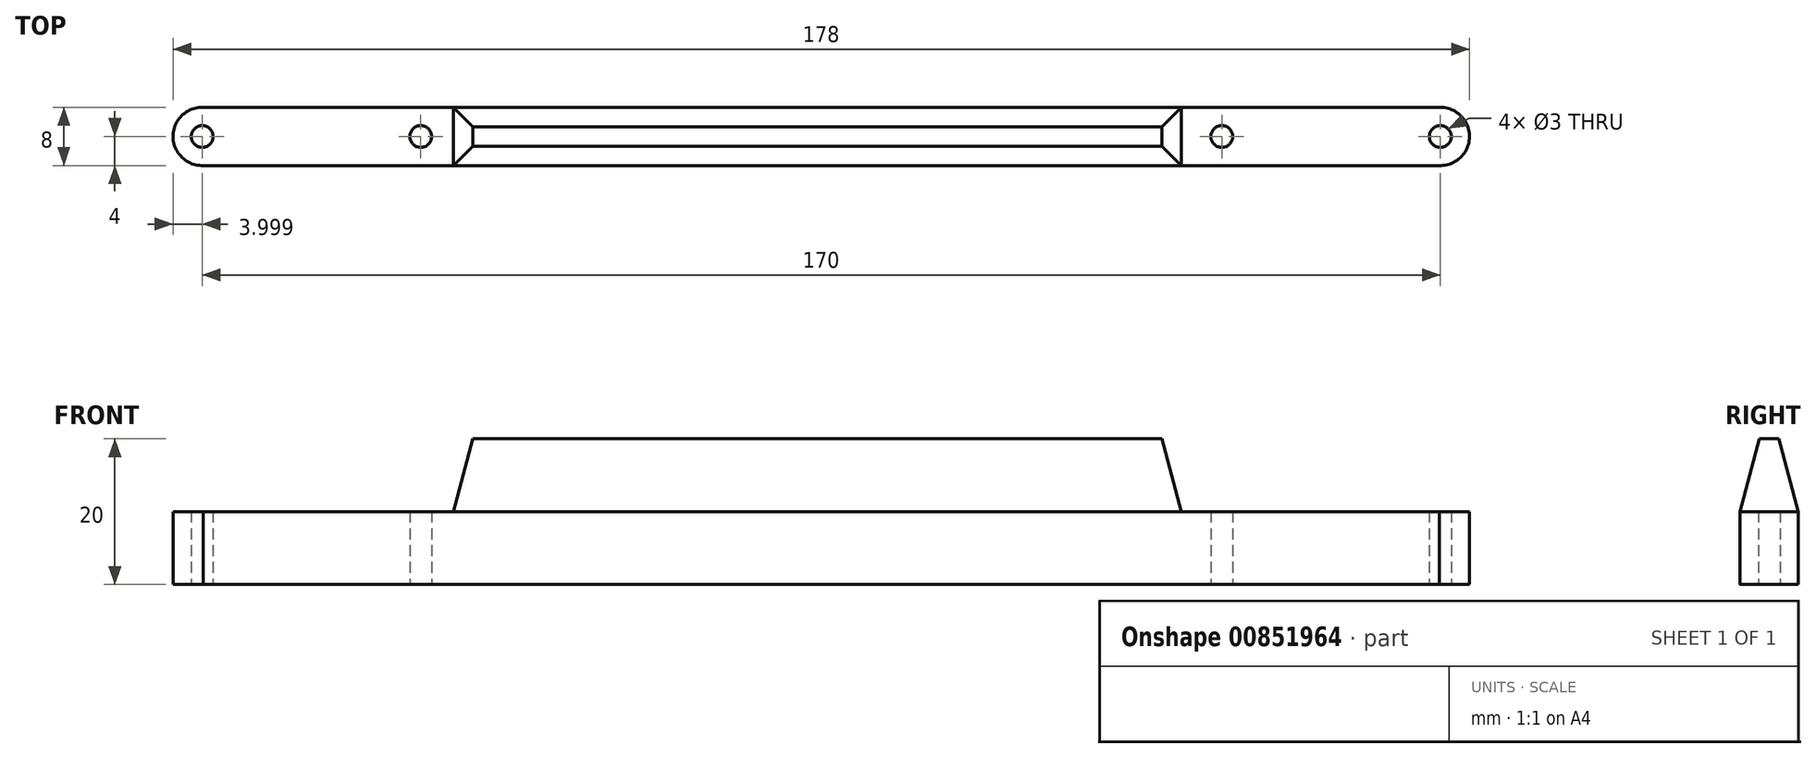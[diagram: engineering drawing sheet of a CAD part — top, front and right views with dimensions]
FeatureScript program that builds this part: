
annotation { "Feature Type Name" : "Feature", "Feature Type Description" : "" }
export const myFeature = defineFeature(function(context is Context, id is Id, definition is map)
    precondition{}
    {
        {
            var Q0;
            Q0=qCreatedBy(makeId("Top.planeOp"),FACE);
            var sketch = newSketch(context, id + "F0", { "sketchPlane" : qUnion([Q0])});
            skCircle(sketch, "E0", {"center": v(55.53, 0) * mm, "radius": 1.5 * mm});
            skCircle(sketch, "E1", {"center": v(-54.47, 0) * mm, "radius": 1.5 * mm});
            skCircle(sketch, "E2", {"center": v(85.53, 0) * mm, "radius": 1.5 * mm});
            skCircle(sketch, "E3", {"center": v(-84.47, 0) * mm, "radius": 1.5 * mm});
            skLineSegment(sketch, "E4", {"start": v(-84.47, 0) * mm, "end": v(-54.47, 0) * mm, "construction": true});
            skLineSegment(sketch, "E5", {"start": v(-54.47, 0) * mm, "end": v(55.53, 0) * mm, "construction": true});
            skLineSegment(sketch, "E6", {"start": v(55.53, 0) * mm, "end": v(85.53, 0) * mm, "construction": true});
            skLineSegment(sketch, "E7", {"start": v(85.53, 0) * mm, "end": v(85.53, 0) * mm});
            skArc(sketch, "E8", {"start": v(-84.42, 4) * mm, "mid": v(-88.47, -0.04) * mm, "end": v(-84.33, -4) * mm});
            skArc(sketch, "E9", {"start": v(85.4, -4) * mm, "mid": v(89.53, -0.07) * mm, "end": v(85.53, 4) * mm});
            skLineSegment(sketch, "E10", {"start": v(-84.42, 4) * mm, "end": v(85.53, 4) * mm});
            skLineSegment(sketch, "E11", {"start": v(85.4, -4) * mm, "end": v(-84.33, -4) * mm});
            skSolve(sketch);
        }
        {
            var Q0;
            Q0 = qSketchRegion(id + "F0", true);
            extrude(context, id + "F1", {"entities" : qUnion([Q0]), "depth" : 10 * mm, "offsetDistance" : 25 * mm});
        }
        {
            var Q0;
            Q0=makeQuery(id+"F1.opExtrude","CAP_FACE",FACE,{"disambiguationData":[OSD([sQuery(id+"F0.wireOp",EDGE,"E0"),sQuery(id+"F0.wireOp",EDGE,"E1"),sQuery(id+"F0.wireOp",EDGE,"E2"),sQuery(id+"F0.wireOp",EDGE,"E3"),sQuery(id+"F0.wireOp",EDGE,"E8"),sQuery(id+"F0.wireOp",EDGE,"E9"),sQuery(id+"F0.wireOp",EDGE,"E10"),sQuery(id+"F0.wireOp",EDGE,"E11")])],"isStart":false});
            var sketch = newSketch(context, id + "F2", { "sketchPlane" : qUnion([Q0])});
            skLineSegment(sketch, "E12.bottom", {"start": v(-50, 4) * mm, "end": v(50, 4) * mm});
            skLineSegment(sketch, "E12.top", {"start": v(-50, -4) * mm, "end": v(50, -4) * mm});
            skLineSegment(sketch, "E12.left", {"start": v(-50, 4) * mm, "end": v(-50, -4) * mm});
            skLineSegment(sketch, "E12.right", {"start": v(50, 4) * mm, "end": v(50, -4) * mm});
            skSolve(sketch);
        }
        {
            var Q0;
            Q0=makeQuery(id+"F2.imprint","IMPRINT",FACE,{"disambiguationData":[TD([[makeQuery(id+"F2.imprint","IMPRINT",EDGE,{"derivedFrom":sQuery(id+"F2.wireOp",EDGE,"E12.bottom")}),-1.0]])]});
            extrude(context, id + "F3", {"entities" : qUnion([Q0]), "operationType" : NewBodyOperationType.ADD, "depth" : 10 * mm, "offsetDistance" : 25 * mm, "hasDraft" : true, "draftAngle" : 15 * degree, "draftPullDirection" : true});
        }
    });
